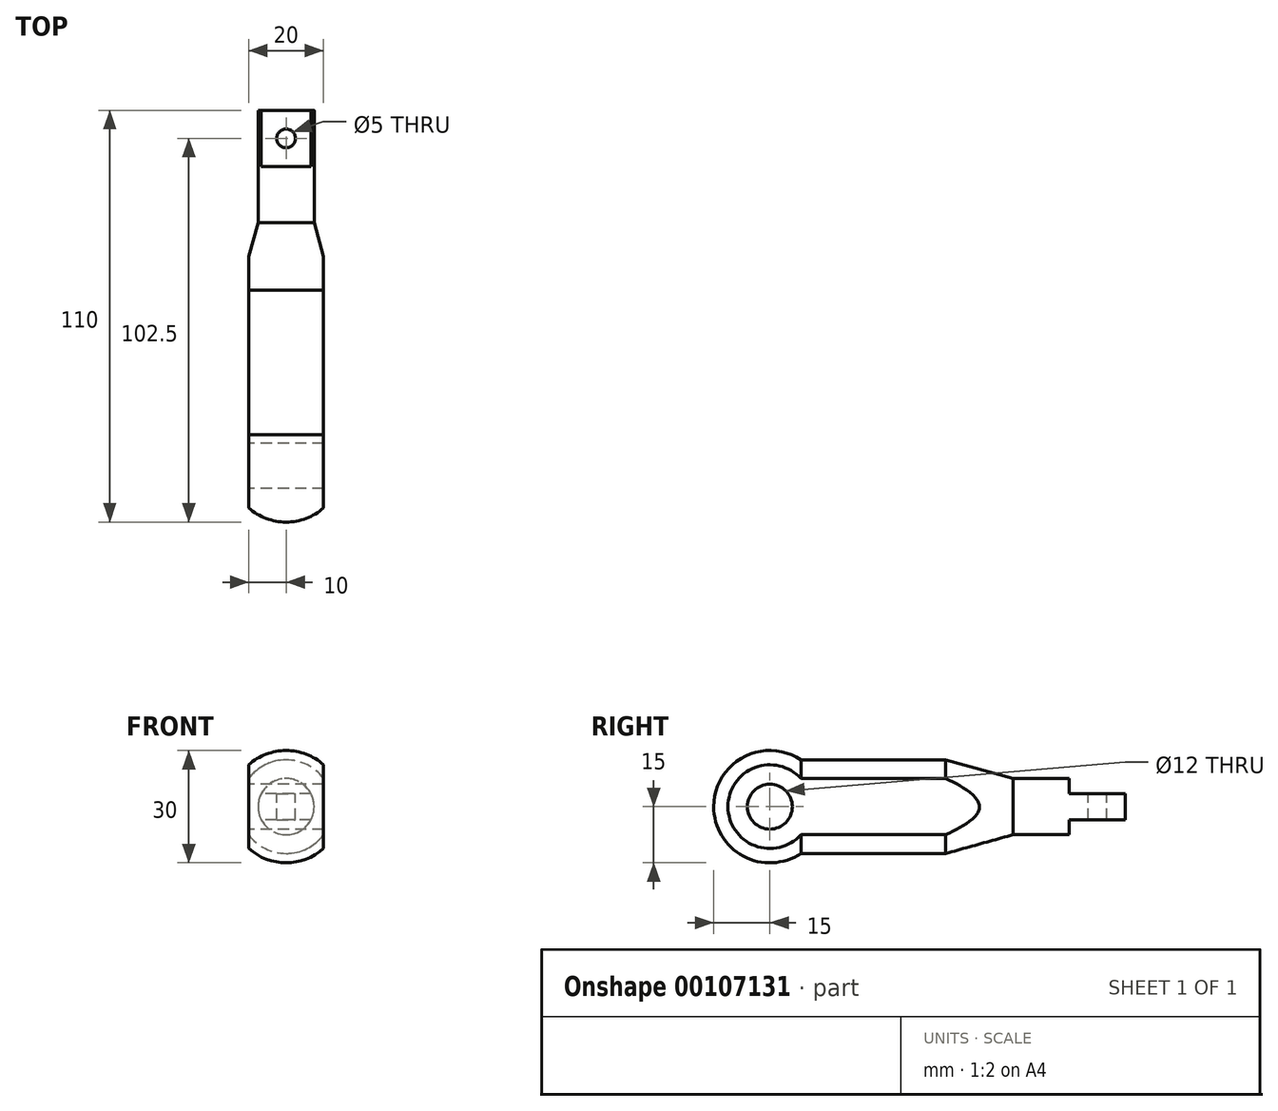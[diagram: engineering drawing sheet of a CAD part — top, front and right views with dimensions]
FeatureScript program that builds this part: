
annotation { "Feature Type Name" : "Feature", "Feature Type Description" : "" }
export const myFeature = defineFeature(function(context is Context, id is Id, definition is map)
    precondition{}
    {
        {
            var Q0;
            Q0=qCreatedBy(makeId("Right.planeOp"),FACE);
            var sketch = newSketch(context, id + "F0", { "sketchPlane" : qUnion([Q0])});
            skLineSegment(sketch, "E0", {"start": v(0, 0) * mm, "end": v(0, 3.5) * mm});
            skLineSegment(sketch, "E1", {"start": v(0, 3.5) * mm, "end": v(-15, 3.5) * mm});
            skLineSegment(sketch, "E2", {"start": v(-15, 3.5) * mm, "end": v(-15, 7.5) * mm});
            skLineSegment(sketch, "E3", {"start": v(-15, 7.5) * mm, "end": v(-30, 7.5) * mm});
            skLineSegment(sketch, "E4", {"start": v(-30, 7.5) * mm, "end": v(-48, 12.5) * mm});
            skLineSegment(sketch, "E5", {"start": v(-48, 12.5) * mm, "end": v(-95, 12.5) * mm});
            skLineSegment(sketch, "E6", {"start": v(0, 0) * mm, "end": v(-84.57, 0) * mm, "construction": true});
            skLineSegment(sketch, "E7", {"start": v(-95, 12.5) * mm, "end": v(-95, 0) * mm});
            skLineSegment(sketch, "E8", {"start": v(-95, 0) * mm, "end": v(0, 0) * mm});
            skLineSegment(sketch, "E9", {"start": v(-48, 12.5) * mm, "end": v(-48, 0) * mm, "construction": true});
            skArc(sketch, "E10", {"start": v(-86.7, 12.5) * mm, "mid": v(-102.1, 13.22) * mm, "end": v(-110, 0) * mm});
            skLineSegment(sketch, "E11", {"start": v(-110, 0) * mm, "end": v(-95, 0) * mm});
            skLineSegment(sketch, "E12", {"start": v(-15, 7.5) * mm, "end": v(0, 7.5) * mm});
            skLineSegment(sketch, "E13", {"start": v(0, 7.5) * mm, "end": v(0, 0) * mm});
            skSolve(sketch);
        }
        {
            var Q0;
            {var subQ0=sQuery(id+"F0.wireOp",EDGE,"E7");Q0=makeQuery(id+"F0.imprint","IMPRINT",FACE,{"disambiguationData":[TD([[makeQuery(id+"F0.imprint","IMPRINT",EDGE,{"derivedFrom":subQ0}),-1.0]])]});}
            var Q1;
            Q1=makeQuery(id+"F0.imprint","IMPRINT",FACE,{"disambiguationData":[TD([[makeQuery(id+"F0.imprint","IMPRINT",EDGE,{"derivedFrom":sQuery(id+"F0.wireOp",EDGE,"E0")}),1.0]])]});
            var Q2;
            Q2=sQuery(id+"F0.wireOp",EDGE,"E8");
            revolve(context, id + "F1", {"entities" : qUnion([Q0, Q1]), "axis" : qUnion([Q2]), "revolveType" : RevolveType.FULL});
        }
        {
            var Q0;
            Q0=qCreatedBy(makeId("Right.planeOp"),FACE);
            var sketch = newSketch(context, id + "F2", { "sketchPlane" : qUnion([Q0])});
            skCircle(sketch, "E14", {"center": v(-95, 0) * mm, "radius": 6 * mm});
            skSolve(sketch);
        }
        {
            var Q0;
            Q0 = qSketchRegion(id + "F0", true);
            var Q1;
            Q1=sQuery(id+"F0.wireOp",EDGE,"E8");
            revolve(context, id + "F3", {"operationType" : NewBodyOperationType.ADD, "entities" : qUnion([Q0]), "axis" : qUnion([Q1]), "revolveType" : RevolveType.FULL});
        }
        {
            var Q0;
            Q0 = qSketchRegion(id + "F2", true);
            extrude(context, id + "F4", {"entities" : qUnion([Q0]), "operationType" : NewBodyOperationType.REMOVE, "endBound" : BoundingType.THROUGH_ALL, "depth" : 25 * mm});
        }
        {
            var Q0;
            Q0 = qSketchRegion(id + "F2", true);
            extrude(context, id + "F5", {"entities" : qUnion([Q0]), "operationType" : NewBodyOperationType.REMOVE, "endBound" : BoundingType.THROUGH_ALL, "oppositeDirection" : true, "depth" : 25 * mm});
        }
        {
            var Q0;
            Q0=qCreatedBy(makeId("Top.planeOp"),FACE);
            var sketch = newSketch(context, id + "F6", { "sketchPlane" : qUnion([Q0])});
            skCircle(sketch, "E15", {"center": v(0, -7.5) * mm, "radius": 2.5 * mm});
            skSolve(sketch);
        }
        {
            var Q0;
            Q0 = qSketchRegion(id + "F6", true);
            extrude(context, id + "F7", {"entities" : qUnion([Q0]), "operationType" : NewBodyOperationType.REMOVE, "endBound" : BoundingType.THROUGH_ALL, "oppositeDirection" : true, "depth" : 25 * mm});
        }
        {
            var Q0;
            Q0 = qSketchRegion(id + "F6", true);
            extrude(context, id + "F8", {"entities" : qUnion([Q0]), "operationType" : NewBodyOperationType.REMOVE, "endBound" : BoundingType.THROUGH_ALL, "depth" : 25 * mm});
        }
        {
            var Q0;
            Q0=qCreatedBy(makeId("Front.planeOp"),FACE);
            var sketch = newSketch(context, id + "F9", { "sketchPlane" : qUnion([Q0])});
            skLineSegment(sketch, "E16.bottom", {"start": v(-23.85, 23.17) * mm, "end": v(-10, 23.17) * mm});
            skLineSegment(sketch, "E16.top", {"start": v(-23.85, -35.29) * mm, "end": v(-10, -35.29) * mm});
            skLineSegment(sketch, "E16.left", {"start": v(-23.85, 23.17) * mm, "end": v(-23.85, -35.29) * mm});
            skLineSegment(sketch, "E16.right", {"start": v(-10, 23.17) * mm, "end": v(-10, -35.29) * mm});
            skLineSegment(sketch, "E17.bottom", {"start": v(21.54, 24.71) * mm, "end": v(10, 24.71) * mm});
            skLineSegment(sketch, "E17.top", {"start": v(21.54, -35.29) * mm, "end": v(10, -35.29) * mm});
            skLineSegment(sketch, "E17.left", {"start": v(21.54, 24.71) * mm, "end": v(21.54, -35.29) * mm});
            skLineSegment(sketch, "E17.right", {"start": v(10, 24.71) * mm, "end": v(10, -35.29) * mm});
            skSolve(sketch);
        }
        {
            var Q0;
            Q0 = qSketchRegion(id + "F9", true);
            extrude(context, id + "F10", {"entities" : qUnion([Q0]), "operationType" : NewBodyOperationType.REMOVE, "endBound" : BoundingType.THROUGH_ALL, "depth" : 25 * mm});
        }
        {
            var Q0;
            Q0=makeQuery(id+"F3.opRevolve","SWEPT_FACE",FACE,{"disambiguationData":[OSD([sQuery(id+"F0.wireOp",EDGE,"E13")])]});
            var sketch = newSketch(context, id + "F11", { "sketchPlane" : qUnion([Q0])});
            skLineSegment(sketch, "E18.bottom", {"start": v(-24.73, -17.8) * mm, "end": v(26.32, -17.8) * mm});
            skLineSegment(sketch, "E18.top", {"start": v(-24.73, -3.5) * mm, "end": v(26.32, -3.5) * mm});
            skLineSegment(sketch, "E18.left", {"start": v(-24.73, -17.8) * mm, "end": v(-24.73, -3.5) * mm});
            skLineSegment(sketch, "E18.right", {"start": v(26.32, -17.8) * mm, "end": v(26.32, -3.5) * mm});
            skLineSegment(sketch, "E19.bottom", {"start": v(-25.47, 3.5) * mm, "end": v(26.07, 3.5) * mm});
            skLineSegment(sketch, "E19.top", {"start": v(-25.47, 16.82) * mm, "end": v(26.07, 16.82) * mm});
            skLineSegment(sketch, "E19.left", {"start": v(-25.47, 3.5) * mm, "end": v(-25.47, 16.82) * mm});
            skLineSegment(sketch, "E19.right", {"start": v(26.07, 3.5) * mm, "end": v(26.07, 16.82) * mm});
            skSolve(sketch);
        }
        {
            var Q0;
            Q0 = qSketchRegion(id + "F11", true);
            extrude(context, id + "F12", {"entities" : qUnion([Q0]), "operationType" : NewBodyOperationType.REMOVE, "oppositeDirection" : true, "depth" : 15 * mm});
        }
    });
